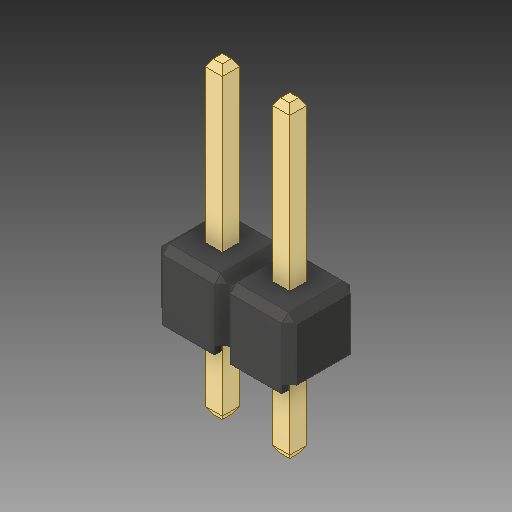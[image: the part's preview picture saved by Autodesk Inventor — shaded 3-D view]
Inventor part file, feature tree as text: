
AUTODESK INVENTOR PART (.ipt)
format: ipt  version: 2019 (Build 230136000, 136)  size: 146,944 bytes
history: native  units: in
note: dims shown in document units (in); Inventor stores cm internally (conversion verified against a paired STEP export)
features: other x3, chamfer x1
ambient origin geometry x8: Origin, YZ Plane, XZ Plane, XY Plane, X Axis, Y Axis, Z Axis, Center Point
bodies: Solid1 (feature_tree), Solid2 (feature_tree), Solid3 (feature_tree), Solid4 (feature_tree)
feature tree (4):
  chamfer  "Chamfer2"  [1 undecoded]
  other  "Boss-Extrude3"
  other  "LPattern1[1]"
  other  "LPattern1[2]"
note: 1 required parameter value undecoded (feature->parameter linkage not recoverable at this tier; creation-order binding heuristic only, values carry confidence <= 0.55)
